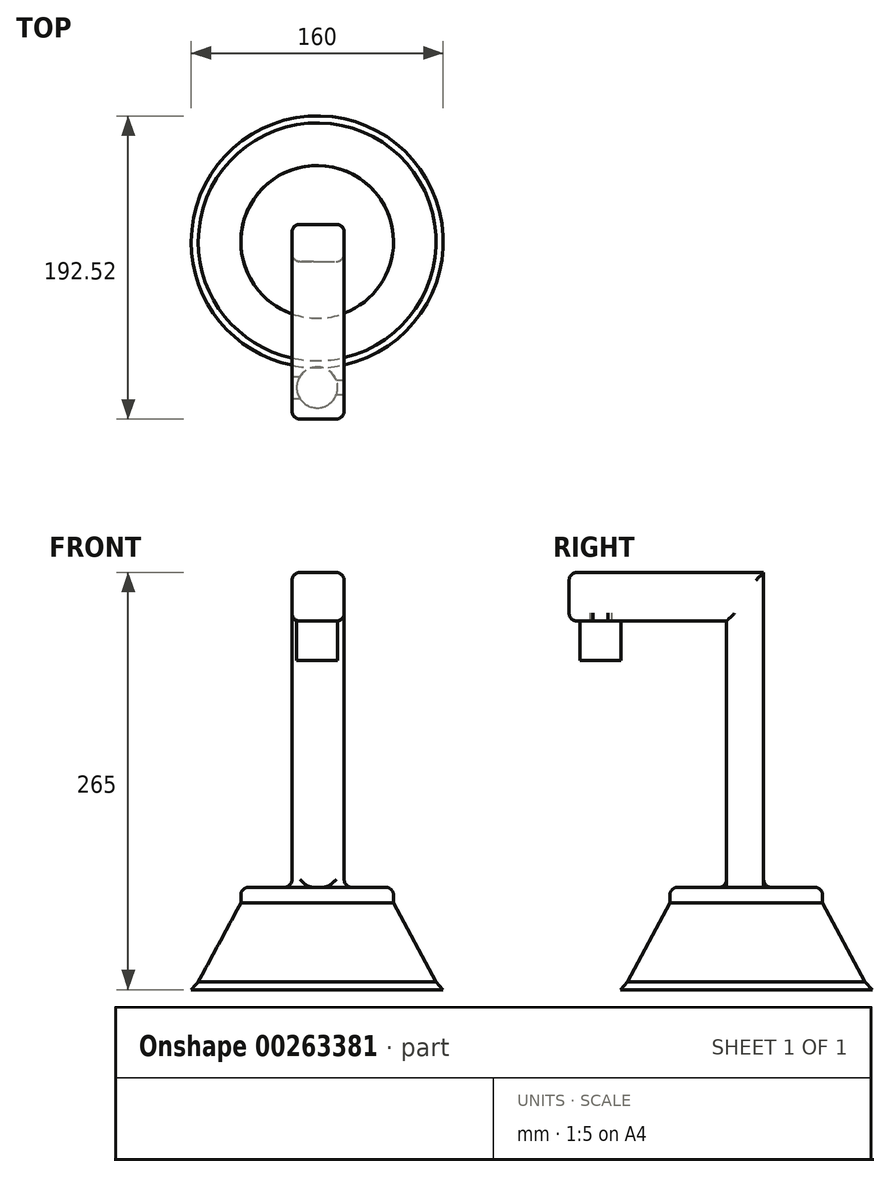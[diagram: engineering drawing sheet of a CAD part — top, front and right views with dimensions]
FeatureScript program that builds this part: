
annotation { "Feature Type Name" : "Feature", "Feature Type Description" : "" }
export const myFeature = defineFeature(function(context is Context, id is Id, definition is map)
    precondition{}
    {
        {
            var Q0;
            Q0=qCreatedBy(makeId("Top.planeOp"),FACE);
            var sketch = newSketch(context, id + "F0", { "sketchPlane" : qUnion([Q0])});
            skCircle(sketch, "E0", {"center": v(0, 0) * mm, "radius": 48.5 * mm});
            skSolve(sketch);
        }
        {
            var Q0;
            Q0=makeQuery(id+"F0.imprint","IMPRINT",FACE,{"disambiguationData":[TD([[makeQuery(id+"F0.imprint","IMPRINT",EDGE,{"derivedFrom":sQuery(id+"F0.wireOp",EDGE,"E0")}),1.0]])]});
            extrude(context, id + "F1", {"entities" : qUnion([Q0]), "oppositeDirection" : true, "depth" : 10 * mm});
        }
        {
            var Q0;
            Q0=makeQuery(id+"F1.opExtrude","CAP_EDGE",EDGE,{"disambiguationData":[OSD([sQuery(id+"F0.wireOp",EDGE,"E0")])],"isStart":true});
            fillet(context, id + "F2", {"entities" : qUnion([Q0]), "radius" : 5 * mm, "tangentPropagation" : true, "allowEdgeOverflow" : false});
        }
        {
            var Q0;
            Q0=makeQuery(id+"F1.opExtrude","CAP_FACE",FACE,{"disambiguationData":[OSD([sQuery(id+"F0.wireOp",EDGE,"E0")])],"isStart":true});
            var sketch = newSketch(context, id + "F3", { "sketchPlane" : qUnion([Q0])});
            skLineSegment(sketch, "E1.bottom", {"start": v(-16.03, 11.04) * mm, "end": v(17.12, 11.04) * mm});
            skLineSegment(sketch, "E1.top", {"start": v(-16.03, -12.52) * mm, "end": v(17.12, -12.52) * mm});
            skLineSegment(sketch, "E1.left", {"start": v(-16.03, 11.04) * mm, "end": v(-16.03, -12.52) * mm});
            skLineSegment(sketch, "E1.right", {"start": v(17.12, 11.04) * mm, "end": v(17.12, -12.52) * mm});
            skSolve(sketch);
        }
        {
            var Q0;
            Q0=makeQuery(id+"F3.imprint","IMPRINT",FACE,{"disambiguationData":[TD([[makeQuery(id+"F3.imprint","IMPRINT",EDGE,{"derivedFrom":sQuery(id+"F3.wireOp",EDGE,"E1.bottom")}),-1.0]])]});
            extrude(context, id + "F4", {"entities" : qUnion([Q0]), "operationType" : NewBodyOperationType.ADD, "depth" : 200 * mm});
        }
        {
            var Q0;
            Q0=makeQuery(id+"F4.opExtrude","SWEPT_FACE",FACE,{"disambiguationData":[OSD([sQuery(id+"F3.wireOp",EDGE,"E1.top")])]});
            var sketch = newSketch(context, id + "F5", { "sketchPlane" : qUnion([Q0])});
            skLineSegment(sketch, "E2.bottom", {"start": v(-16.03, 200) * mm, "end": v(17.12, 200) * mm});
            skLineSegment(sketch, "E2.top", {"start": v(-16.03, 169.13) * mm, "end": v(17.12, 169.13) * mm});
            skLineSegment(sketch, "E2.left", {"start": v(-16.03, 200) * mm, "end": v(-16.03, 169.13) * mm});
            skLineSegment(sketch, "E2.right", {"start": v(17.12, 200) * mm, "end": v(17.12, 169.13) * mm});
            skSolve(sketch);
        }
        {
            var Q0;
            Q0=makeQuery(id+"F5.imprint","IMPRINT",FACE,{"disambiguationData":[TD([[makeQuery(id+"F5.imprint","IMPRINT",EDGE,{"derivedFrom":sQuery(id+"F5.wireOp",EDGE,"E2.bottom")}),-1.0]])]});
            extrude(context, id + "F6", {"entities" : qUnion([Q0]), "operationType" : NewBodyOperationType.ADD, "depth" : 100 * mm});
        }
        {
            var Q0;
            Q0=makeQuery(id+"F6.opExtrude","SWEPT_FACE",FACE,{"disambiguationData":[OSD([sQuery(id+"F5.wireOp",EDGE,"E2.top")])]});
            var sketch = newSketch(context, id + "F7", { "sketchPlane" : qUnion([Q0])});
            skCircle(sketch, "E3", {"center": v(0, 92.5) * mm, "radius": 13 * mm});
            skSolve(sketch);
        }
        {
            var Q0;
            Q0=makeQuery(id+"F7.imprint","IMPRINT",FACE,{"disambiguationData":[TD([[makeQuery(id+"F7.imprint","IMPRINT",EDGE,{"derivedFrom":sQuery(id+"F7.wireOp",EDGE,"E3")}),1.0]])]});
            extrude(context, id + "F8", {"entities" : qUnion([Q0]), "operationType" : NewBodyOperationType.ADD, "depth" : 25 * mm});
        }
        {
            var Q0;
            Q0=makeQuery(id+"F6.boolean.opBoolean","MERGE",FACE,{"derivedFrom":[makeQuery(id+"F4.opExtrude","SWEPT_FACE",FACE,{"disambiguationData":[OSD([sQuery(id+"F3.wireOp",EDGE,"E1.right")])]}),makeQuery(id+"F6.opExtrude","SWEPT_FACE",FACE,{"disambiguationData":[OSD([sQuery(id+"F5.wireOp",EDGE,"E2.right")])]})]});
            var Q1;
            Q1=makeQuery(id+"F6.boolean.opBoolean","MERGE",FACE,{"derivedFrom":[makeQuery(id+"F4.opExtrude","SWEPT_FACE",FACE,{"disambiguationData":[OSD([sQuery(id+"F3.wireOp",EDGE,"E1.left")])]}),makeQuery(id+"F6.opExtrude","SWEPT_FACE",FACE,{"disambiguationData":[OSD([sQuery(id+"F5.wireOp",EDGE,"E2.left")])]})]});
            var Q2;
            Q2=makeQuery(id+"F6.opExtrude","CAP_FACE",FACE,{"disambiguationData":[OSD([sQuery(id+"F5.wireOp",EDGE,"E2.bottom"),sQuery(id+"F5.wireOp",EDGE,"E2.top"),sQuery(id+"F5.wireOp",EDGE,"E2.left"),sQuery(id+"F5.wireOp",EDGE,"E2.right")])],"isStart":false});
            fillet(context, id + "F9", {"entities" : qUnion([Q0, Q1, Q2]), "radius" : 5 * mm, "tangentPropagation" : true, "allowEdgeOverflow" : false});
        }
        {
            var Q0;
            Q0=makeQuery(id+"F1.opExtrude","CAP_FACE",FACE,{"disambiguationData":[OSD([sQuery(id+"F0.wireOp",EDGE,"E0")])],"isStart":false});
            cPlane(context, id + "F10", {"entities" : qUnion([Q0]), "cplaneType" : CPlaneType.OFFSET, "offset" : 50 * mm, "width" : 150 * mm, "height" : 150 * mm});
        }
        {
            var Q0;
            Q0=qCreatedBy(id+"F10.planeOp",FACE);
            var sketch = newSketch(context, id + "F11", { "sketchPlane" : qUnion([Q0])});
            skCircle(sketch, "E4", {"center": v(0, 0) * mm, "radius": 75.5 * mm});
            skSolve(sketch);
        }
        {
            var Q1;
            Q1=makeQuery(id+"F1.opExtrude","CAP_FACE",FACE,{"disambiguationData":[OSD([sQuery(id+"F0.wireOp",EDGE,"E0")])],"isStart":false});
            var Q2;
            Q2=makeQuery(id+"F11.imprint","IMPRINT",FACE,{"disambiguationData":[TD([[makeQuery(id+"F11.imprint","IMPRINT",EDGE,{"derivedFrom":sQuery(id+"F11.wireOp",EDGE,"E4")}),1.0]])]});
            loft(context, id + "F12", {"operationType" : NewBodyOperationType.ADD, "sheetProfilesArray" : [{ "sheetProfileEntities" : qUnion([Q1]) }, { "sheetProfileEntities" : qUnion([Q2]) }]});
        }
        {
            var Q0;
            Q0=qCreatedBy(id+"F10.planeOp",FACE);
            cPlane(context, id + "F13", {"entities" : qUnion([Q0]), "cplaneType" : CPlaneType.OFFSET, "offset" : 5 * mm, "width" : 150 * mm, "height" : 150 * mm});
        }
        {
            var Q0;
            Q0=qCreatedBy(id+"F13.planeOp",FACE);
            var sketch = newSketch(context, id + "F14", { "sketchPlane" : qUnion([Q0])});
            skCircle(sketch, "E5", {"center": v(0, 0) * mm, "radius": 80 * mm});
            skSolve(sketch);
        }
        {
            var Q1;
            Q1=makeQuery(id+"F12.opLoft","CAP_FACE",FACE,{"disambiguationData":[OSD([makeQuery(id+"F11.imprint","IMPRINT",FACE,{"disambiguationData":[TD([[makeQuery(id+"F11.imprint","IMPRINT",EDGE,{"derivedFrom":sQuery(id+"F11.wireOp",EDGE,"E4")}),1.0]])]})])],"isStart":true});
            var Q2;
            Q2=makeQuery(id+"F14.imprint","IMPRINT",FACE,{"disambiguationData":[TD([[makeQuery(id+"F14.imprint","IMPRINT",EDGE,{"derivedFrom":sQuery(id+"F14.wireOp",EDGE,"E5")}),1.0]])]});
            loft(context, id + "F15", {"operationType" : NewBodyOperationType.ADD, "sheetProfilesArray" : [{ "sheetProfileEntities" : qUnion([Q1]) }, { "sheetProfileEntities" : qUnion([Q2]) }]});
        }
    });
